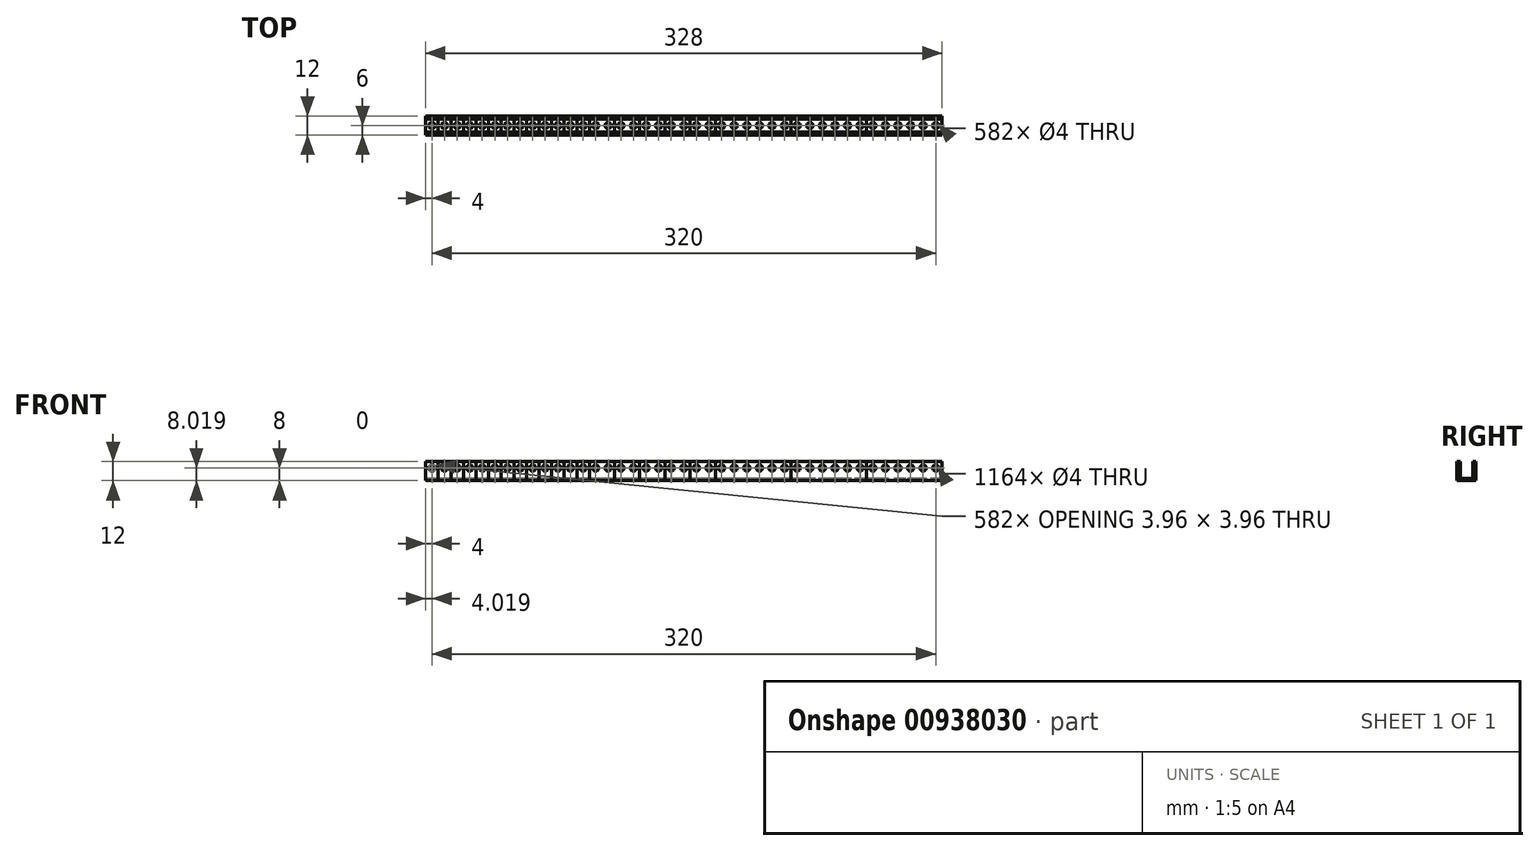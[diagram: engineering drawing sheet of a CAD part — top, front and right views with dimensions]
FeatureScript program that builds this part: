
annotation { "Feature Type Name" : "Feature", "Feature Type Description" : "" }
export const myFeature = defineFeature(function(context is Context, id is Id, definition is map)
    precondition{}
    {
        {
            var Q0;
            Q0=qCreatedBy(makeId("Right.planeOp"),FACE);
            var sketch = newSketch(context, id + "F0", { "sketchPlane" : qUnion([Q0]) });
            skLineSegment(sketch, "E0.bottom", {"start": v(0, 0) * mm, "end": v(12, 0) * mm});
            skLineSegment(sketch, "E0.top", {"start": v(0, 12) * mm, "end": v(2, 12) * mm});
            skLineSegment(sketch, "E0.left", {"start": v(0, 0) * mm, "end": v(0, 12) * mm});
            skLineSegment(sketch, "E0.right", {"start": v(12, 0) * mm, "end": v(12, 12) * mm});
            skLineSegment(sketch, "E1.top", {"start": v(2, 1.5) * mm, "end": v(10, 1.5) * mm});
            skLineSegment(sketch, "E1.left", {"start": v(2, 12) * mm, "end": v(2, 1.5) * mm});
            skLineSegment(sketch, "E1.right", {"start": v(10, 12) * mm, "end": v(10, 1.5) * mm});
            skLineSegment(sketch, "E2.trimOffspring", {"start": v(10, 12) * mm, "end": v(12, 12) * mm});
            skSolve(sketch);
        }
        {
            var Q0;
            Q0=qSketchRegion(id+"F0",true);
            extrude(context, id + "F1", {"entities" : qUnion([Q0]), "depth" : 8 * mm, "offsetDistance" : 25 * mm});
        }
        {
            var Q0;
            Q0=qSketchRegion(id+"F0",true);
            extrude(context, id + "F2", {"entities" : qUnion([Q0]), "depth" : 16 * mm, "offsetDistance" : 25 * mm});
        }
        {
            var Q0;
            Q0=qSketchRegion(id+"F0",true);
            extrude(context, id + "F3", {"entities" : qUnion([Q0]), "depth" : 24 * mm, "offsetDistance" : 25 * mm});
        }
        {
            var Q0;
            Q0=qSketchRegion(id+"F0",true);
            extrude(context, id + "F4", {"entities" : qUnion([Q0]), "depth" : 32 * mm, "offsetDistance" : 25 * mm});
        }
        {
            var Q0;
            Q0=qSketchRegion(id+"F0",true);
            extrude(context, id + "F5", {"entities" : qUnion([Q0]), "depth" : 40 * mm, "offsetDistance" : 25 * mm});
        }
        {
            var Q0;
            Q0=qSketchRegion(id+"F0",true);
            extrude(context, id + "F6", {"entities" : qUnion([Q0]), "depth" : 48 * mm, "offsetDistance" : 25 * mm});
        }
        {
            var Q0;
            Q0=qSketchRegion(id+"F0",true);
            extrude(context, id + "F7", {"entities" : qUnion([Q0]), "depth" : 56 * mm, "offsetDistance" : 25 * mm});
        }
        {
            var Q0;
            Q0=qSketchRegion(id+"F0",true);
            extrude(context, id + "F8", {"entities" : qUnion([Q0]), "depth" : 64 * mm, "offsetDistance" : 25 * mm});
        }
        {
            var Q0;
            Q0=qSketchRegion(id+"F0",true);
            extrude(context, id + "F9", {"entities" : qUnion([Q0]), "depth" : 72 * mm, "offsetDistance" : 25 * mm});
        }
        {
            var Q0;
            Q0=qSketchRegion(id+"F0",true);
            extrude(context, id + "F10", {"entities" : qUnion([Q0]), "depth" : 80 * mm, "offsetDistance" : 25 * mm});
        }
        {
            var Q0;
            Q0=qSketchRegion(id+"F0",true);
            extrude(context, id + "F11", {"entities" : qUnion([Q0]), "depth" : 88 * mm, "offsetDistance" : 25 * mm});
        }
        {
            var Q0;
            Q0=qSketchRegion(id+"F0",true);
            extrude(context, id + "F12", {"entities" : qUnion([Q0]), "depth" : 96 * mm, "offsetDistance" : 25 * mm});
        }
        {
            var Q0;
            Q0=qSketchRegion(id+"F0",true);
            extrude(context, id + "F13", {"entities" : qUnion([Q0]), "depth" : 104 * mm, "offsetDistance" : 25 * mm});
        }
        {
            var Q0;
            Q0=qSketchRegion(id+"F0",true);
            extrude(context, id + "F14", {"entities" : qUnion([Q0]), "depth" : 120 * mm, "offsetDistance" : 25 * mm});
        }
        {
            var Q0;
            Q0=qSketchRegion(id+"F0",true);
            extrude(context, id + "F15", {"entities" : qUnion([Q0]), "depth" : 136 * mm, "offsetDistance" : 25 * mm});
        }
        {
            var Q0;
            Q0=qSketchRegion(id+"F0",true);
            extrude(context, id + "F16", {"entities" : qUnion([Q0]), "depth" : 152 * mm, "offsetDistance" : 25 * mm});
        }
        {
            var Q0;
            Q0=qSketchRegion(id+"F0",true);
            extrude(context, id + "F17", {"entities" : qUnion([Q0]), "depth" : 168 * mm, "offsetDistance" : 25 * mm});
        }
        {
            var Q0;
            Q0=qSketchRegion(id+"F0",true);
            extrude(context, id + "F18", {"entities" : qUnion([Q0]), "depth" : 184 * mm, "offsetDistance" : 25 * mm});
        }
        {
            var Q0;
            Q0=qSketchRegion(id+"F0",true);
            extrude(context, id + "F19", {"entities" : qUnion([Q0]), "depth" : 232 * mm, "offsetDistance" : 25 * mm});
        }
        {
            var Q0;
            Q0=qSketchRegion(id+"F0",true);
            extrude(context, id + "F20", {"entities" : qUnion([Q0]), "depth" : 280 * mm, "offsetDistance" : 25 * mm});
        }
        {
            var Q0;
            Q0=qSketchRegion(id+"F0",true);
            extrude(context, id + "F21", {"entities" : qUnion([Q0]), "depth" : 328 * mm, "offsetDistance" : 25 * mm});
        }
        {
            var Q0;
            Q0=qCreatedBy(makeId("Front.planeOp"),FACE);
            var sketch = newSketch(context, id + "F22", { "sketchPlane" : qUnion([Q0]) });
            skLineSegment(sketch, "E3.bottom", {"start": v(0, 0) * mm, "end": v(4, 0) * mm, "construction": true});
            skLineSegment(sketch, "E3.top", {"start": v(0, 8) * mm, "end": v(4, 8) * mm, "construction": true});
            skLineSegment(sketch, "E3.left", {"start": v(0, 0) * mm, "end": v(0, 8) * mm, "construction": true});
            skLineSegment(sketch, "E3.right", {"start": v(4, 0) * mm, "end": v(4, 8) * mm, "construction": true});
            skCircle(sketch, "E4", {"center": v(4, 8) * mm, "radius": 2 * mm});
            skCircle(sketch, "E5.1.0.0", {"center": v(12, 8) * mm, "radius": 2 * mm});
            skCircle(sketch, "E5.2.0.0", {"center": v(20, 8) * mm, "radius": 2 * mm});
            skLineSegment(sketch, "E5.direction1", {"start": v(4, 8) * mm, "end": v(12, 8) * mm, "construction": true});
            skCircle(sketch, "E6.0.3.0", {"center": v(28, 8) * mm, "radius": 2 * mm});
            skCircle(sketch, "E6.0.4.0", {"center": v(36, 8) * mm, "radius": 2 * mm});
            skCircle(sketch, "E6.0.5.0", {"center": v(44, 8) * mm, "radius": 2 * mm});
            skCircle(sketch, "E6.0.6.0", {"center": v(52, 8) * mm, "radius": 2 * mm});
            skCircle(sketch, "E6.0.7.0", {"center": v(60, 8) * mm, "radius": 2 * mm});
            skCircle(sketch, "E6.0.8.0", {"center": v(68, 8) * mm, "radius": 2 * mm});
            skCircle(sketch, "E6.0.9.0", {"center": v(76, 8) * mm, "radius": 2 * mm});
            skCircle(sketch, "E6.0.10.0", {"center": v(84, 8) * mm, "radius": 2 * mm});
            skCircle(sketch, "E6.0.11.0", {"center": v(92, 8) * mm, "radius": 2 * mm});
            skCircle(sketch, "E6.0.12.0", {"center": v(100, 8) * mm, "radius": 2 * mm});
            skCircle(sketch, "E6.0.13.0", {"center": v(108, 8) * mm, "radius": 2 * mm});
            skCircle(sketch, "E6.0.14.0", {"center": v(116, 8) * mm, "radius": 2 * mm});
            skCircle(sketch, "E6.0.15.0", {"center": v(124, 8) * mm, "radius": 2 * mm});
            skCircle(sketch, "E6.0.16.0", {"center": v(132, 8) * mm, "radius": 2 * mm});
            skCircle(sketch, "E6.0.17.0", {"center": v(140, 8) * mm, "radius": 2 * mm});
            skCircle(sketch, "E6.0.18.0", {"center": v(148, 8) * mm, "radius": 2 * mm});
            skCircle(sketch, "E6.0.19.0", {"center": v(156, 8) * mm, "radius": 2 * mm});
            skCircle(sketch, "E6.0.20.0", {"center": v(164, 8) * mm, "radius": 2 * mm});
            skCircle(sketch, "E6.0.21.0", {"center": v(172, 8) * mm, "radius": 2 * mm});
            skCircle(sketch, "E6.0.22.0", {"center": v(180, 8) * mm, "radius": 2 * mm});
            skCircle(sketch, "E6.0.23.0", {"center": v(188, 8) * mm, "radius": 2 * mm});
            skCircle(sketch, "E6.0.24.0", {"center": v(196, 8) * mm, "radius": 2 * mm});
            skCircle(sketch, "E6.0.25.0", {"center": v(204, 8) * mm, "radius": 2 * mm});
            skCircle(sketch, "E6.0.26.0", {"center": v(212, 8) * mm, "radius": 2 * mm});
            skCircle(sketch, "E6.0.27.0", {"center": v(220, 8) * mm, "radius": 2 * mm});
            skCircle(sketch, "E6.0.28.0", {"center": v(228, 8) * mm, "radius": 2 * mm});
            skCircle(sketch, "E6.0.29.0", {"center": v(236, 8) * mm, "radius": 2 * mm});
            skCircle(sketch, "E6.0.30.0", {"center": v(244, 8) * mm, "radius": 2 * mm});
            skCircle(sketch, "E6.0.31.0", {"center": v(252, 8) * mm, "radius": 2 * mm});
            skCircle(sketch, "E6.0.32.0", {"center": v(260, 8) * mm, "radius": 2 * mm});
            skCircle(sketch, "E6.0.33.0", {"center": v(268, 8) * mm, "radius": 2 * mm});
            skCircle(sketch, "E6.0.34.0", {"center": v(276, 8) * mm, "radius": 2 * mm});
            skCircle(sketch, "E6.0.35.0", {"center": v(284, 8) * mm, "radius": 2 * mm});
            skCircle(sketch, "E6.0.36.0", {"center": v(292, 8) * mm, "radius": 2 * mm});
            skCircle(sketch, "E6.0.37.0", {"center": v(300, 8) * mm, "radius": 2 * mm});
            skCircle(sketch, "E6.0.38.0", {"center": v(308, 8) * mm, "radius": 2 * mm});
            skCircle(sketch, "E6.0.39.0", {"center": v(316, 8) * mm, "radius": 2 * mm});
            skCircle(sketch, "E6.0.40.0", {"center": v(324, 8) * mm, "radius": 2 * mm});
            skSolve(sketch);
        }
        {
            var Q0;
            Q0=qSketchRegion(id+"F22",true);
            extrude(context, id + "F23", {"entities" : qUnion([Q0]), "operationType" : NewBodyOperationType.REMOVE, "endBound" : BoundingType.THROUGH_ALL, "oppositeDirection" : true, "depth" : 25 * mm, "offsetDistance" : 25 * mm});
        }
        {
            var Q0;
            Q0=qCreatedBy(makeId("Top.planeOp"),FACE);
            var sketch = newSketch(context, id + "F24", { "sketchPlane" : qUnion([Q0]) });
            skPoint(sketch, "E7.0", {"position": v(0, 12) * mm});
            skLineSegment(sketch, "E8.bottom", {"start": v(0, 12) * mm, "end": v(4, 12) * mm, "construction": true});
            skLineSegment(sketch, "E8.top", {"start": v(0, 0) * mm, "end": v(4, 0) * mm, "construction": true});
            skLineSegment(sketch, "E8.left", {"start": v(0, 12) * mm, "end": v(0, 0) * mm, "construction": true});
            skLineSegment(sketch, "E8.right", {"start": v(4, 12) * mm, "end": v(4, 0) * mm, "construction": true});
            skCircle(sketch, "E9", {"center": v(4, 6) * mm, "radius": 2 * mm});
            skCircle(sketch, "E10.1.0.0", {"center": v(12, 6) * mm, "radius": 2 * mm});
            skCircle(sketch, "E10.2.0.0", {"center": v(20, 6) * mm, "radius": 2 * mm});
            skCircle(sketch, "E10.3.0.0", {"center": v(28, 6) * mm, "radius": 2 * mm});
            skCircle(sketch, "E10.4.0.0", {"center": v(36, 6) * mm, "radius": 2 * mm});
            skCircle(sketch, "E10.5.0.0", {"center": v(44, 6) * mm, "radius": 2 * mm});
            skCircle(sketch, "E10.6.0.0", {"center": v(52, 6) * mm, "radius": 2 * mm});
            skCircle(sketch, "E10.7.0.0", {"center": v(60, 6) * mm, "radius": 2 * mm});
            skCircle(sketch, "E10.8.0.0", {"center": v(68, 6) * mm, "radius": 2 * mm});
            skCircle(sketch, "E10.9.0.0", {"center": v(76, 6) * mm, "radius": 2 * mm});
            skCircle(sketch, "E10.10.0.0", {"center": v(84, 6) * mm, "radius": 2 * mm});
            skCircle(sketch, "E10.11.0.0", {"center": v(92, 6) * mm, "radius": 2 * mm});
            skCircle(sketch, "E10.12.0.0", {"center": v(100, 6) * mm, "radius": 2 * mm});
            skCircle(sketch, "E10.13.0.0", {"center": v(108, 6) * mm, "radius": 2 * mm});
            skCircle(sketch, "E10.14.0.0", {"center": v(116, 6) * mm, "radius": 2 * mm});
            skCircle(sketch, "E10.15.0.0", {"center": v(124, 6) * mm, "radius": 2 * mm});
            skCircle(sketch, "E10.16.0.0", {"center": v(132, 6) * mm, "radius": 2 * mm});
            skCircle(sketch, "E10.17.0.0", {"center": v(140, 6) * mm, "radius": 2 * mm});
            skCircle(sketch, "E10.18.0.0", {"center": v(148, 6) * mm, "radius": 2 * mm});
            skCircle(sketch, "E10.19.0.0", {"center": v(156, 6) * mm, "radius": 2 * mm});
            skCircle(sketch, "E10.20.0.0", {"center": v(164, 6) * mm, "radius": 2 * mm});
            skCircle(sketch, "E10.21.0.0", {"center": v(172, 6) * mm, "radius": 2 * mm});
            skCircle(sketch, "E10.22.0.0", {"center": v(180, 6) * mm, "radius": 2 * mm});
            skCircle(sketch, "E10.23.0.0", {"center": v(188, 6) * mm, "radius": 2 * mm});
            skCircle(sketch, "E10.24.0.0", {"center": v(196, 6) * mm, "radius": 2 * mm});
            skCircle(sketch, "E10.25.0.0", {"center": v(204, 6) * mm, "radius": 2 * mm});
            skCircle(sketch, "E10.26.0.0", {"center": v(212, 6) * mm, "radius": 2 * mm});
            skCircle(sketch, "E10.27.0.0", {"center": v(220, 6) * mm, "radius": 2 * mm});
            skCircle(sketch, "E10.28.0.0", {"center": v(228, 6) * mm, "radius": 2 * mm});
            skCircle(sketch, "E10.29.0.0", {"center": v(236, 6) * mm, "radius": 2 * mm});
            skCircle(sketch, "E10.30.0.0", {"center": v(244, 6) * mm, "radius": 2 * mm});
            skCircle(sketch, "E10.31.0.0", {"center": v(252, 6) * mm, "radius": 2 * mm});
            skCircle(sketch, "E10.32.0.0", {"center": v(260, 6) * mm, "radius": 2 * mm});
            skCircle(sketch, "E10.33.0.0", {"center": v(268, 6) * mm, "radius": 2 * mm});
            skCircle(sketch, "E10.34.0.0", {"center": v(276, 6) * mm, "radius": 2 * mm});
            skCircle(sketch, "E10.35.0.0", {"center": v(284, 6) * mm, "radius": 2 * mm});
            skCircle(sketch, "E10.36.0.0", {"center": v(292, 6) * mm, "radius": 2 * mm});
            skCircle(sketch, "E10.37.0.0", {"center": v(300, 6) * mm, "radius": 2 * mm});
            skCircle(sketch, "E10.38.0.0", {"center": v(308, 6) * mm, "radius": 2 * mm});
            skCircle(sketch, "E10.39.0.0", {"center": v(316, 6) * mm, "radius": 2 * mm});
            skCircle(sketch, "E10.40.0.0", {"center": v(324, 6) * mm, "radius": 2 * mm});
            skLineSegment(sketch, "E10.direction1", {"start": v(4, 6) * mm, "end": v(12, 6) * mm, "construction": true});
            skSolve(sketch);
        }
        {
            var Q0;
            Q0=qSketchRegion(id+"F24",true);
            extrude(context, id + "F25", {"entities" : qUnion([Q0]), "operationType" : NewBodyOperationType.REMOVE, "endBound" : BoundingType.THROUGH_ALL, "depth" : 25 * mm, "offsetDistance" : 25 * mm});
        }
    });
